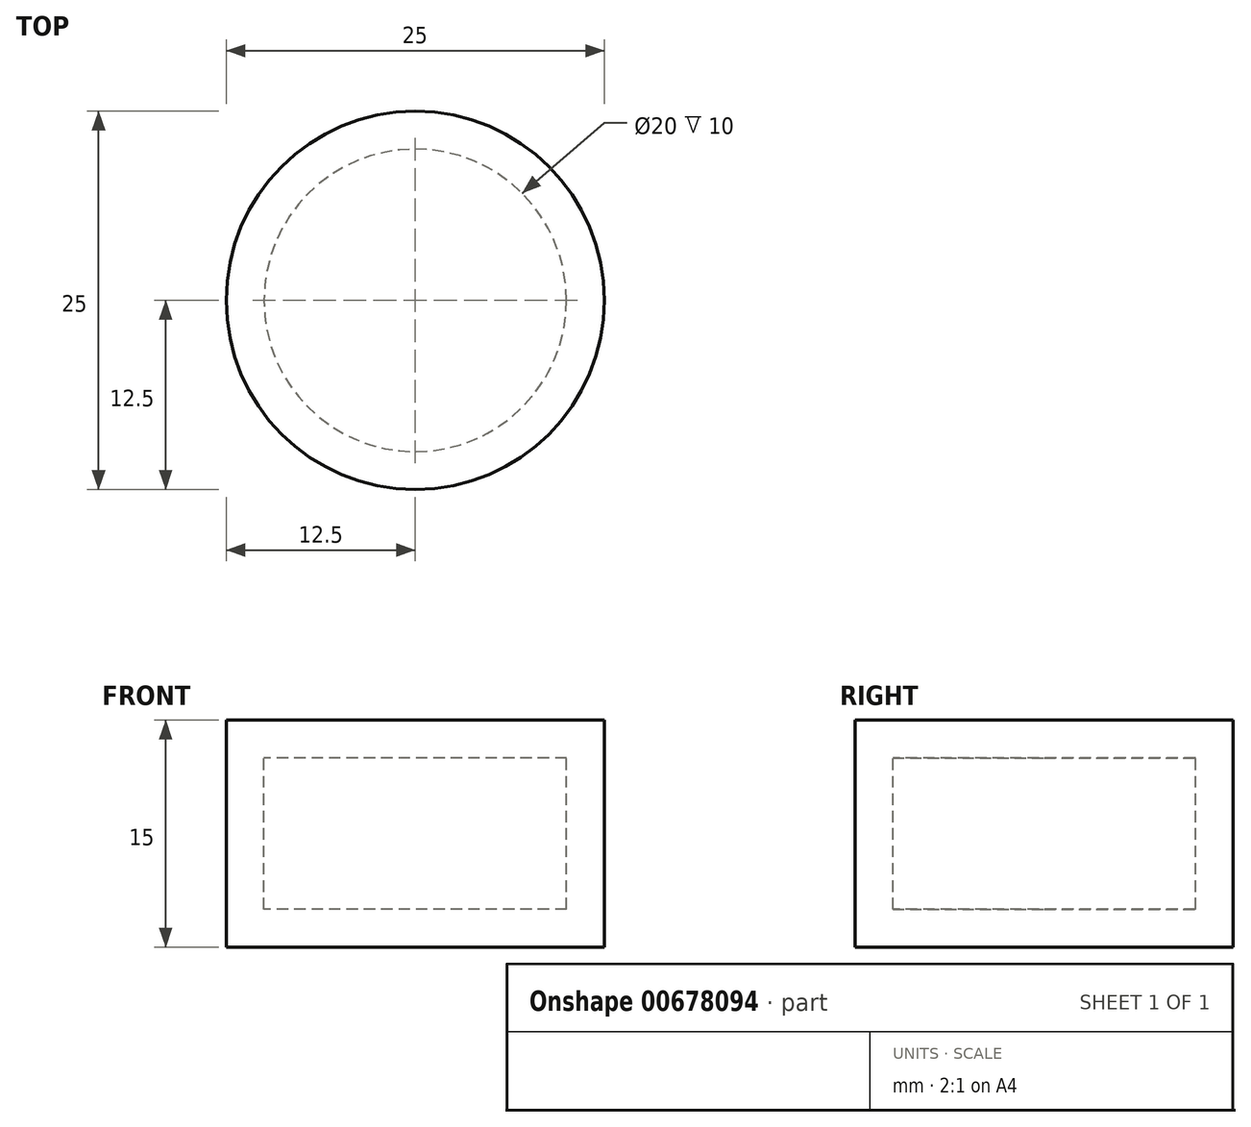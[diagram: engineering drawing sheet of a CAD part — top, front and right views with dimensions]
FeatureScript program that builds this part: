
annotation { "Feature Type Name" : "Feature", "Feature Type Description" : "" }
export const myFeature = defineFeature(function(context is Context, id is Id, definition is map)
    precondition{}
    {
        {
            var Q0;
            Q0=qCreatedBy(makeId("Top.planeOp"),FACE);
            var sketch = newSketch(context, id + "F0", { "sketchPlane" : qUnion([Q0])});
            skCircle(sketch, "E0", {"center": v(0, 0) * mm, "radius": 12.5 * mm});
            skLineSegment(sketch, "E1", {"start": v(-4.12, 11.8) * mm, "end": v(-4.12, 19.74) * mm});
            skLineSegment(sketch, "E2", {"start": v(-4.12, 19.74) * mm, "end": v(0, 19.74) * mm});
            skLineSegment(sketch, "E3.MirrorCS", {"start": v(4.12, 19.74) * mm, "end": v(0, 19.74) * mm});
            skLineSegment(sketch, "E4.MirrorCS", {"start": v(4.12, 11.8) * mm, "end": v(4.12, 19.74) * mm});
            skSolve(sketch);
        }
        {
            var Q0;
            {var subQ0=sQuery(id+"F0.wireOp",EDGE,"E0");var subQ1=makeQuery(id+"F0.imprint","INTERSECT",VERTEX,{"derivedFrom":[subQ0,sQuery(id+"F0.wireOp",EDGE,"E1")]});Q0=makeQuery(id+"F0.imprint","IMPRINT",FACE,{"disambiguationData":[TD([[makeQuery(id+"F0.imprint","IMPRINT",EDGE,{"disambiguationData":[TD([[subQ1,1.0]])],"derivedFrom":subQ0}),1.0]])]});}
            extrude(context, id + "F1", {"entities" : qUnion([Q0]), "oppositeDirection" : true, "depth" : 15 * mm, "offsetDistance" : 25.4 * mm});
        }
        {
            var Q0;
            Q0=makeQuery(id+"F1.opExtrude","SWEPT_FACE",FACE,{"disambiguationData":[OSD([sQuery(id+"F0.wireOp",EDGE,"E0")])]});
            var Q1;
            Q1=makeQuery(id+"F1.opExtrude","SWEPT_BODY",BODY,{"disambiguationData":[OSD([sQuery(id+"F0.wireOp",EDGE,"E0")])]});
            shell(context, id + "F2", {"isHollow" : true, "entities" : qUnion([Q0]), "parts" : qUnion([Q1]), "thickness" : 2.5 * mm});
        }
    });
